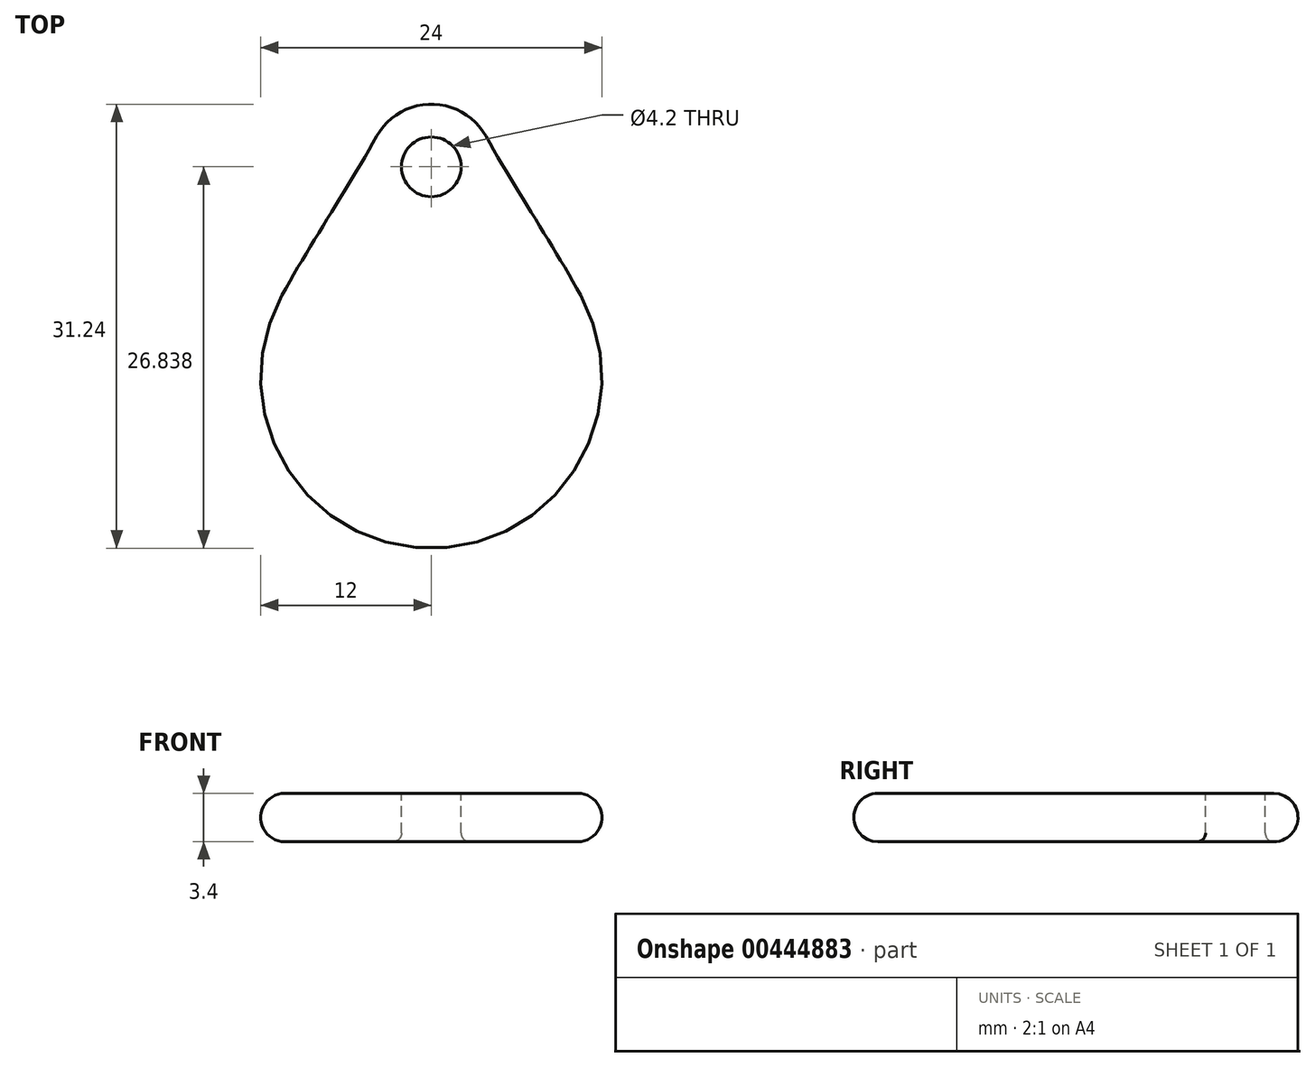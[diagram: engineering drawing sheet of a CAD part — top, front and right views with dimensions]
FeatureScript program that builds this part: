
annotation { "Feature Type Name" : "Feature", "Feature Type Description" : "" }
export const myFeature = defineFeature(function(context is Context, id is Id, definition is map)
    precondition{}
    {
        {
            var Q0;
            Q0=qCreatedBy(makeId("Top.planeOp"),FACE);
            var sketch = newSketch(context, id + "F0", { "sketchPlane" : qUnion([Q0])});
            skCircle(sketch, "E0", {"center": v(0, 0) * mm, "radius": 12 * mm});
            skLineSegment(sketch, "E1", {"start": v(0, 0) * mm, "end": v(0, 26) * mm});
            skFitSpline(sketch, "E2", {"points": [v(0, 26) * mm, v(-10.5, 5.8) * mm], "startDerivative": vector(-3.4, -17.62) * mm, "endDerivative": vector(-9.63, -17.47) * mm});
            skFitSpline(sketch, "E3.MirrorCS", {"points": [v(0, 26) * mm, v(10.5, 5.8) * mm], "startDerivative": vector(3.4, -17.62) * mm, "endDerivative": vector(9.63, -17.47) * mm});
            skSolve(sketch);
        }
        {
            var Q0;
            {var subQ0=sQuery(id+"F0.wireOp",EDGE,"E3.MirrorCS");Q0=makeQuery(id+"F0.imprint","IMPRINT",FACE,{"disambiguationData":[TD([[makeQuery(id+"F0.imprint","IMPRINT",EDGE,{"derivedFrom":subQ0}),-1.0]])]});}
            var Q1;
            {var subQ0=sQuery(id+"F0.wireOp",EDGE,"E0");var subQ1=makeQuery(id+"F0.imprint","INTERSECT",VERTEX,{"derivedFrom":[subQ0,sQuery(id+"F0.wireOp",EDGE,"E3.MirrorCS")]});Q1=makeQuery(id+"F0.imprint","IMPRINT",FACE,{"disambiguationData":[TD([[makeQuery(id+"F0.imprint","IMPRINT",EDGE,{"disambiguationData":[TD([[subQ1,-1.0]])],"derivedFrom":subQ0}),1.0]])]});}
            var Q2;
            {var subQ0=sQuery(id+"F0.wireOp",EDGE,"E2");Q2=makeQuery(id+"F0.imprint","IMPRINT",FACE,{"disambiguationData":[TD([[makeQuery(id+"F0.imprint","IMPRINT",EDGE,{"derivedFrom":subQ0}),1.0]])]});}
            extrude(context, id + "F1", {"entities" : qUnion([Q0, Q1, Q2]), "depth" : 3.4 * mm});
        }
        {
            var Q0;
            Q0=makeQuery(id+"F1.opExtrude","SWEPT_EDGE",EDGE,{"disambiguationData":[OSD([sQuery(id+"F0.wireOp",EDGE,"E1"),sQuery(id+"F0.wireOp",EDGE,"E2"),sQuery(id+"F0.wireOp",EDGE,"E3.MirrorCS")])]});
            fillet(context, id + "F2", {"entities" : qUnion([Q0]), "radius" : 4.4 * mm, "tangentPropagation" : true, "allowEdgeOverflow" : false});
        }
        {
            var Q0;
            Q0=makeQuery(id+"F1.opExtrude","CAP_FACE",FACE,{"disambiguationData":[OSD([sQuery(id+"F0.wireOp",EDGE,"E0"),sQuery(id+"F0.wireOp",EDGE,"E2"),sQuery(id+"F0.wireOp",EDGE,"E3.MirrorCS")])],"isStart":false});
            var sketch = newSketch(context, id + "F3", { "sketchPlane" : qUnion([Q0])});
            skCircle(sketch, "E4", {"center": v(0, 14.84) * mm, "radius": 2.1 * mm});
            skSolve(sketch);
        }
        {
            var Q0;
            Q0=makeQuery(id+"F3.imprint","IMPRINT",FACE,{"disambiguationData":[TD([[makeQuery(id+"F3.imprint","IMPRINT",EDGE,{"derivedFrom":sQuery(id+"F3.wireOp",EDGE,"E4")}),1.0]])]});
            extrude(context, id + "F4", {"entities" : qUnion([Q0]), "operationType" : NewBodyOperationType.REMOVE, "oppositeDirection" : true, "depth" : 25 * mm});
        }
        {
            var Q0;
            Q0=makeQuery(id+"F1.opExtrude","CAP_EDGE",EDGE,{"disambiguationData":[OSD([sQuery(id+"F0.wireOp",EDGE,"E2")])],"isStart":false});
            var Q1;
            {var subQ0=sQuery(id+"F0.wireOp",EDGE,"E3.MirrorCS");var subQ1=sQuery(id+"F0.wireOp",EDGE,"E2");Q1=makeQuery(id+"F2.opFillet","BLEND_EDGE",EDGE,{"blendedFrom":[makeQuery(id+"F1.opExtrude","SWEPT_EDGE",EDGE,{"disambiguationData":[OSD([sQuery(id+"F0.wireOp",EDGE,"E1"),subQ1,subQ0])]}),makeQuery(id+"F1.opExtrude","CAP_FACE",FACE,{"disambiguationData":[OSD([sQuery(id+"F0.wireOp",EDGE,"E0"),subQ1,subQ0])],"isStart":true})],"blendedInto":[makeQuery(id+"F1.opExtrude","CAP_FACE",FACE,{"disambiguationData":[OSD([sQuery(id+"F0.wireOp",EDGE,"E0"),subQ1,subQ0])],"isStart":true})]});}
            fillet(context, id + "F5", {"entities" : qUnion([Q0, Q1]), "radius" : 1.7 * mm, "tangentPropagation" : true, "allowEdgeOverflow" : false});
        }
        {
            var Q0;
            Q0=makeQuery(id+"F4.boolean.opBoolean","INTERSECT",EDGE,{"derivedFrom":[makeQuery(id+"F1.opExtrude","CAP_FACE",FACE,{"disambiguationData":[OSD([sQuery(id+"F0.wireOp",EDGE,"E0"),sQuery(id+"F0.wireOp",EDGE,"E2"),sQuery(id+"F0.wireOp",EDGE,"E3.MirrorCS")])],"isStart":true}),makeQuery(id+"F4.opExtrude","SWEPT_FACE",FACE,{"disambiguationData":[OSD([sQuery(id+"F3.wireOp",EDGE,"E4")])]})]});
            var Q1;
            Q1=makeQuery(id+"F4.boolean.opBoolean","COPY",EDGE,{"derivedFrom":makeQuery(id+"F4.opExtrude","CAP_EDGE",EDGE,{"disambiguationData":[OSD([sQuery(id+"F3.wireOp",EDGE,"E4")])],"isStart":true})});
            fillet(context, id + "F6", {"entities" : qUnion([Q0, Q1]), "radius" : 0.6 * mm, "tangentPropagation" : true, "allowEdgeOverflow" : false});
        }
    });
